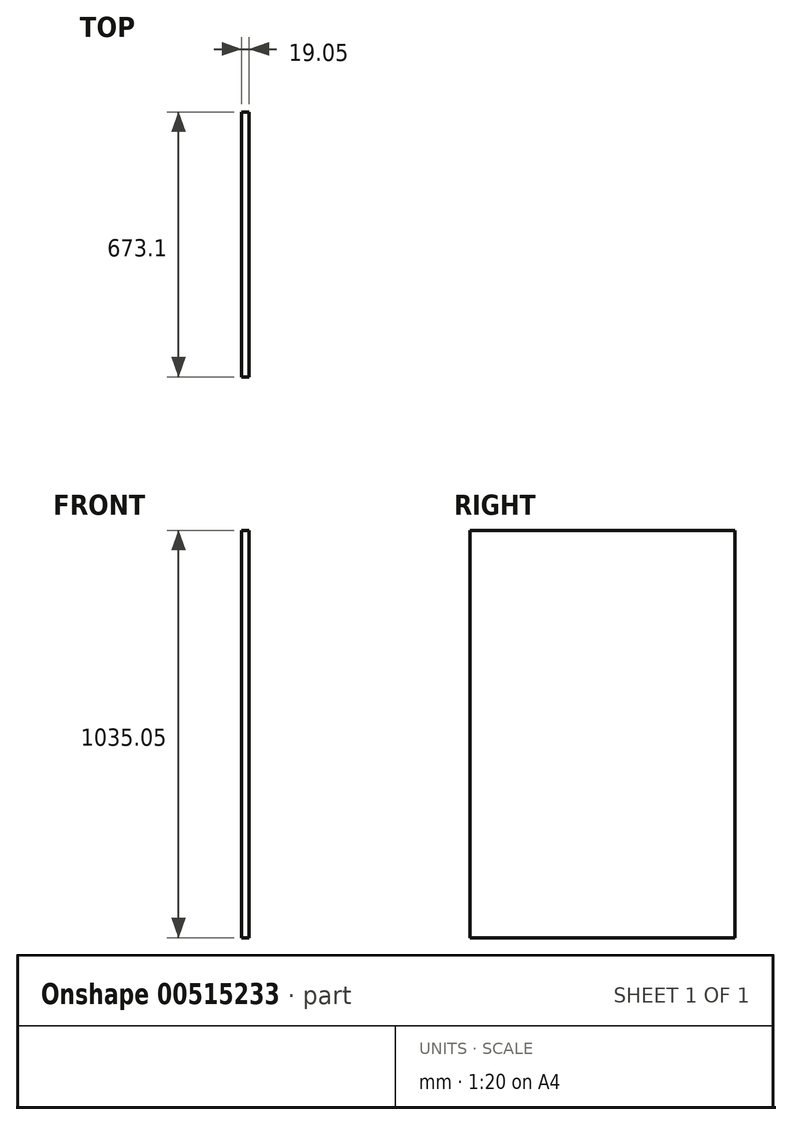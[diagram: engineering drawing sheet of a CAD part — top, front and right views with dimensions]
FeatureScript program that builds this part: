
annotation { "Feature Type Name" : "Feature", "Feature Type Description" : "" }
export const myFeature = defineFeature(function(context is Context, id is Id, definition is map)
    precondition{}
    {
        {
            var Q0;
            Q0=qCreatedBy(makeId("Right.planeOp"),FACE);
            var sketch = newSketch(context, id + "F0", { "sketchPlane" : qUnion([Q0])});
            skLineSegment(sketch, "E0.bottom", {"start": v(336.55, 352.43) * mm, "end": v(-336.55, 352.43) * mm});
            skLineSegment(sketch, "E0.top", {"start": v(336.55, -352.43) * mm, "end": v(-336.55, -352.43) * mm});
            skLineSegment(sketch, "E0.left", {"start": v(336.55, 352.43) * mm, "end": v(336.55, -352.43) * mm});
            skLineSegment(sketch, "E0.right", {"start": v(-336.55, 352.43) * mm, "end": v(-336.55, -352.43) * mm});
            skPoint(sketch, "E0.middle", {"position": v(0, 0) * mm});
            skSolve(sketch);
        }
        {
            var Q0;
            Q0=qSketchRegion(id+"F0",true);
            extrude(context, id + "F1", {"entities" : qUnion([Q0]), "flatOperationType" : FlatOperationType.REMOVE, "offsetDistance" : 25.4 * mm, "depth" : 19.05 * mm, "domain" : OperationDomain.MODEL});
        }
        {
            var Q0;
            Q0=makeQuery(id+"F1.opExtrude","SWEPT_FACE",FACE,{"disambiguationData":[OSD([sQuery(id+"F0.wireOp",EDGE,"E0.bottom")])]});
            extrude(context, id + "F2", {"entities" : qUnion([Q0]), "operationType" : NewBodyOperationType.ADD, "flatOperationType" : FlatOperationType.REMOVE, "offsetDistance" : 25.4 * mm, "depth" : 330.2 * mm, "domain" : OperationDomain.MODEL});
        }
    });
